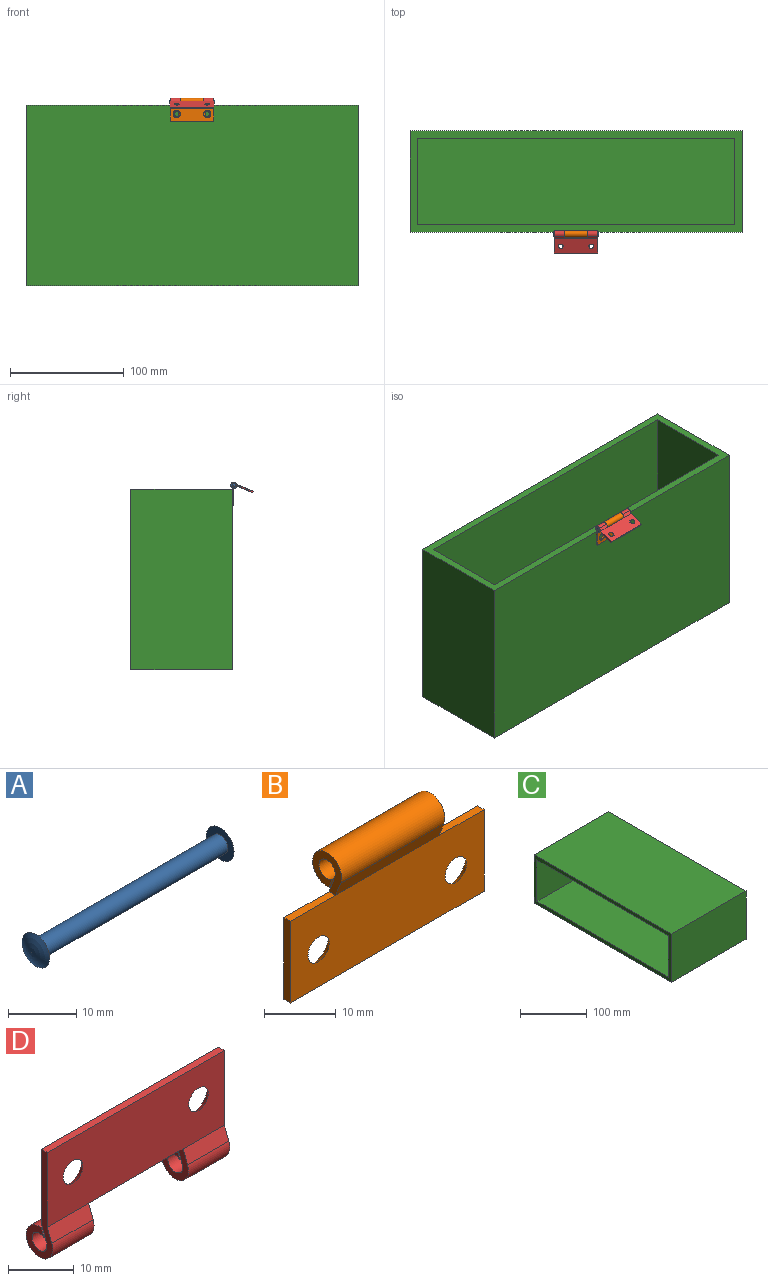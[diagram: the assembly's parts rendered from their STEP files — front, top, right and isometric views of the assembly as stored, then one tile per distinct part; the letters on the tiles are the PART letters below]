
ASSEMBLY  parts=4 mates=3
PART A: 5 faces, bbox 39.8x5.7x5.7 mm
  f0: cylinder r=1.59mm len=38.1mm, axis (1,0,0), area 380mm2, adj f1,f3
  f1: plane 5.72x5.72mm, normal (1,0,0), area 17.7mm2, adj f0,f2
  f2: sphere r=5.25mm, area 27.9mm2, adj f1
  f3: plane 5.72x5.72mm, normal (-1,0,0), area 17.7mm2, adj f0,f4
  f4: sphere r=5.25mm, area 27.9mm2, adj f3
PART B: 16 faces, bbox 38.1x5.7x20.3 mm
  f0: plane 6.43x5.72mm, normal (-1,0,0), area 18.8mm2, adj f4,f5,f6,f7,f8,f12
  f1: plane 6.43x5.72mm, normal (1,0,0), area 18.8mm2, adj f4,f5,f6,f7,f8,f11
  f2: plane 38.1x1.27mm, normal (0,0,-1), area 48.4mm2, adj f3,f9,f10,f13
  f3: plane 38.1x13.89mm, normal (0,1,0), area 465mm2, adj f2,f4,f10,f11,f12,f13,f14,f15
  f4: plane 20.32x3.03mm, normal (0,0.94,0.34), area 65.5mm2, adj f0,f1,f3,f5
  f5: cylinder r=1.59mm len=20.32mm, axis (1,0,0), area 184.2mm2, adj f0,f1,f4,f6
  f6: plane 20.32x1.57mm, normal (0,-0.94,-0.34), area 33.9mm2, adj f0,f1,f5,f7
  f7: cylinder r=2.86mm len=20.32mm, axis (1,0,0), area 303.4mm2, adj f0,f1,f6,f8
  f8: plane 20.32x2.53mm, normal (0,-0.93,-0.36), area 55.2mm2, adj f0,f1,f7,f9
  f9: plane 38.1x13.89mm, normal (0,-1,0), area 501.7mm2, adj f2,f8,f10,f11,f12,f13,f14,f15
  f10: plane 13.89x1.27mm, normal (1,0,0), area 17.6mm2, adj f2,f3,f9,f11
  f11: plane 8.89x1.27mm, normal (0,0,1), area 11.3mm2, adj f1,f3,f9,f10
  f12: plane 8.89x1.27mm, normal (0,0,1), area 11.3mm2, adj f0,f3,f9,f13
  f13: plane 13.89x1.27mm, normal (-1,0,0), area 17.6mm2, adj f2,f3,f9,f12
  f14: cone r=3.2mm half-angle=41deg, axis (0,1,0), area 28mm2, adj f3,f9
  f15: cone r=3.2mm half-angle=41deg, axis (0,1,0), area 28mm2, adj f3,f9
PART C: 11 faces, bbox 158.8x292.1x88.9 mm
  f0: plane 279.4x76.2mm, normal (-1,0,0), area 21290.3mm2, adj f1,f2,f8,f10
  f1: plane 152.4x76.2mm, normal (0,-1,0), area 11612.9mm2, adj f0,f8,f9,f10
  f2: plane 152.4x76.2mm, normal (0,1,0), area 11612.9mm2, adj f0,f8,f9,f10
  f3: plane 292.1x158.75mm, normal (0,0,1), area 46370.9mm2, adj f4,f5,f6,f9
  f4: plane 292.1x88.9mm, normal (1,0,0), area 25967.7mm2, adj f3,f5,f6,f7
  f5: plane 158.75x88.9mm, normal (0,1,0), area 14112.9mm2, adj f3,f4,f7,f9
  f6: plane 158.75x88.9mm, normal (0,-1,0), area 14112.9mm2, adj f3,f4,f7,f9
  f7: plane 292.1x158.75mm, normal (0,0,-1), area 46370.9mm2, adj f4,f5,f6,f9
  f8: plane 279.4x152.4mm, normal (0,0,1), area 42580.6mm2, adj f0,f1,f2,f9
  f9: plane 292.1x88.9mm, normal (-1,0,0), area 4677.4mm2, adj f1,f2,f3,f5,f6,f7,f8,f10
  f10: plane 279.4x152.4mm, normal (0,0,-1), area 42580.6mm2, adj f0,f1,f2,f9
PART D: 20 faces, bbox 38.1x5.7x20.3 mm
  f0: cylinder r=2.86mm len=8.89mm, axis (-1,0,0), area 132.7mm2, adj f6,f12,f13,f17
  f1: plane 8.89x1.57mm, normal (0,-0.94,0.34), area 14.8mm2, adj f2,f5,f14,f16
  f2: cylinder r=1.59mm len=8.89mm, axis (-1,0,0), area 80.6mm2, adj f1,f3,f14,f16
  f3: plane 8.89x3.03mm, normal (0,0.94,-0.34), area 28.6mm2, adj f2,f9,f14,f16
  f4: plane 8.89x2.53mm, normal (0,-0.93,0.36), area 24.2mm2, adj f5,f11,f14,f16
  f5: cylinder r=2.86mm len=8.89mm, axis (-1,0,0), area 132.7mm2, adj f1,f4,f14,f16
  f6: plane 8.89x1.57mm, normal (0,-0.94,0.34), area 14.8mm2, adj f0,f7,f13,f17
  f7: cylinder r=1.59mm len=8.89mm, axis (-1,0,0), area 80.6mm2, adj f6,f8,f13,f17
  f8: plane 8.89x3.03mm, normal (0,0.94,-0.34), area 28.6mm2, adj f7,f9,f13,f17
  f9: plane 38.1x13.89mm, normal (0,1,0), area 465mm2, adj f3,f8,f10,f13,f14,f15,f18,f19
  f10: plane 38.1x1.27mm, normal (0,0,1), area 48.4mm2, adj f9,f11,f13,f14
  f11: plane 38.1x13.89mm, normal (0,-1,0), area 501.7mm2, adj f4,f10,f12,f13,f14,f15,f18,f19
  f12: plane 8.89x2.53mm, normal (0,-0.93,0.36), area 24.2mm2, adj f0,f11,f13,f17
  f13: plane 20.32x5.72mm, normal (1,0,0), area 36.5mm2, adj f0,f6,f7,f8,f9,f10,f11,f12
  f14: plane 20.32x5.72mm, normal (-1,0,0), area 36.5mm2, adj f1,f2,f3,f4,f5,f9,f10,f11
  f15: plane 20.32x1.27mm, normal (0,0,-1), area 25.8mm2, adj f9,f11,f16,f17
  f16: plane 6.43x5.72mm, normal (1,0,0), area 18.8mm2, adj f1,f2,f3,f4,f5,f15
  f17: plane 6.43x5.72mm, normal (-1,0,0), area 18.8mm2, adj f0,f6,f7,f8,f12,f15
  f18: cone r=3.2mm half-angle=41deg, axis (0,1,0), area 28mm2, adj f9,f11
  f19: cone r=3.2mm half-angle=41deg, axis (0,1,0), area 28mm2, adj f9,f11
PLACE A rot(axis=(0,0,-1),180deg) t=(195.2,9.96,38.86)mm
PLACE B rot(axis=(0,0,1),180deg) t=(195.2,9.96,38.86)mm
PLACE C rot(axis=(0.58,0.58,-0.58),120deg) t=(195.2,100.54,41.65)mm fixed
PLACE D rot(axis=(0,-0.83,0.56),180deg) t=(195.2,9.96,38.86)mm
MATE revolute D.f0 <-> A.f0  axis (1,0,0) through (176.15,9.96,38.86)mm
MATE fastened A.f0 <-> B.f5  axis (-1,0,0) through (195.2,9.96,38.86)mm
MATE fastened B.f9 <-> C.f3  axis (0,1,0) through (195.2,11.64,35.3)mm
